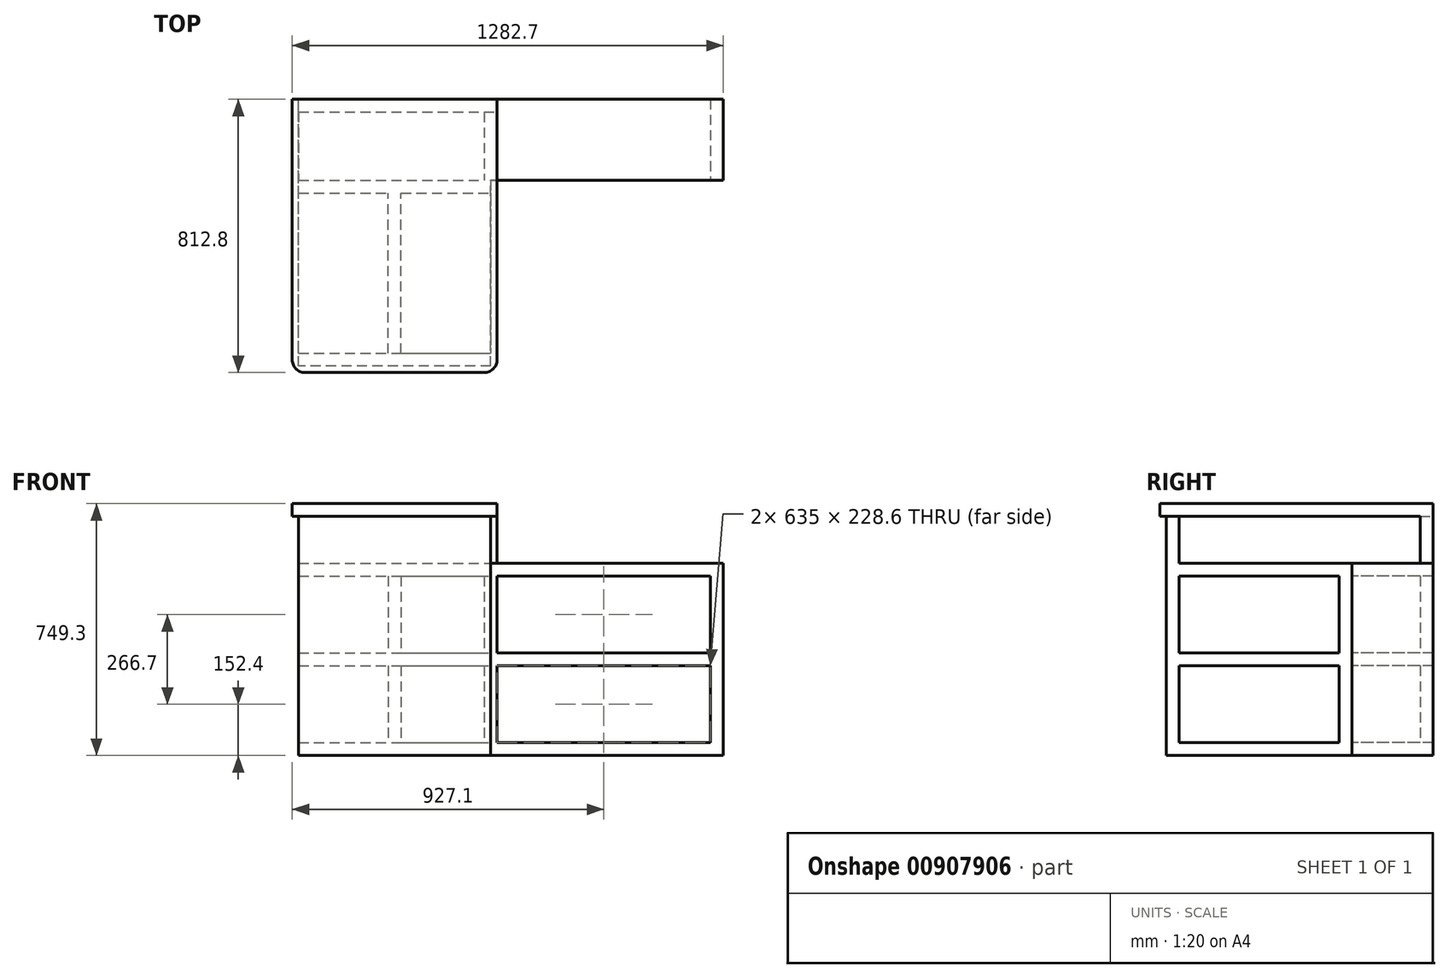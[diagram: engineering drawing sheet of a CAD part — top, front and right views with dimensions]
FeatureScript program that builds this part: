
annotation { "Feature Type Name" : "Feature", "Feature Type Description" : "" }
export const myFeature = defineFeature(function(context is Context, id is Id, definition is map)
    precondition{}
    {
        {
            var Q0;
            Q0=qCreatedBy(makeId("Top.planeOp"),FACE);
            var sketch = newSketch(context, id + "F0", { "sketchPlane" : qUnion([Q0])});
            skLineSegment(sketch, "E0.bottom", {"start": v(266.7, -406.4) * mm, "end": v(-266.7, -406.4) * mm});
            skLineSegment(sketch, "E0.top", {"start": v(304.8, 406.4) * mm, "end": v(-304.8, 406.4) * mm});
            skLineSegment(sketch, "E0.left", {"start": v(304.8, -368.3) * mm, "end": v(304.8, 165.1) * mm});
            skLineSegment(sketch, "E0.right", {"start": v(-304.8, -368.3) * mm, "end": v(-304.8, 406.4) * mm});
            skPoint(sketch, "E0.middle", {"position": v(0, 0) * mm});
            skLineSegment(sketch, "E1.bottom", {"start": v(304.8, 406.4) * mm, "end": v(977.9, 406.4) * mm});
            skLineSegment(sketch, "E1.top", {"start": v(304.8, 165.1) * mm, "end": v(977.9, 165.1) * mm});
            skLineSegment(sketch, "E1.right", {"start": v(977.9, 406.4) * mm, "end": v(977.9, 165.1) * mm});
            skLineSegment(sketch, "E2.0", {"start": v(958.85, 406.4) * mm, "end": v(958.85, 184.15) * mm});
            skLineSegment(sketch, "E2.1", {"start": v(-285.75, -387.35) * mm, "end": v(-285.75, 406.4) * mm});
            skLineSegment(sketch, "E2.2", {"start": v(285.75, -387.35) * mm, "end": v(-285.75, -387.35) * mm});
            skLineSegment(sketch, "E2.3", {"start": v(285.75, -387.35) * mm, "end": v(285.75, 184.15) * mm});
            skLineSegment(sketch, "E2.4", {"start": v(285.75, 184.15) * mm, "end": v(958.85, 184.15) * mm});
            skLineSegment(sketch, "E3.0", {"start": v(-330.2, -431.8) * mm, "end": v(-330.2, 406.4) * mm});
            skLineSegment(sketch, "E3.1", {"start": v(330.2, -431.8) * mm, "end": v(-330.2, -431.8) * mm});
            skLineSegment(sketch, "E3.2", {"start": v(330.2, -431.8) * mm, "end": v(330.2, 139.7) * mm});
            skLineSegment(sketch, "E3.3", {"start": v(330.2, 139.7) * mm, "end": v(977.9, 139.7) * mm});
            skLineSegment(sketch, "E4", {"start": v(977.9, 165.1) * mm, "end": v(977.9, 139.7) * mm});
            skLineSegment(sketch, "E5", {"start": v(304.8, 406.4) * mm, "end": v(304.8, 165.1) * mm});
            skLineSegment(sketch, "E6", {"start": v(-330.2, 406.4) * mm, "end": v(-304.8, 406.4) * mm});
            skPoint(sketch, "E7.visualSharp", {"position": v(-304.8, -406.4) * mm});
            skArc(sketch, "E7.filletArc", {"start": v(-304.8, -368.3) * mm, "mid": v(-293.64, -395.24) * mm, "end": v(-266.7, -406.4) * mm});
            skPoint(sketch, "E8.visualSharp", {"position": v(304.8, -406.4) * mm});
            skArc(sketch, "E8.filletArc", {"start": v(266.7, -406.4) * mm, "mid": v(293.64, -395.24) * mm, "end": v(304.8, -368.3) * mm});
            skLineSegment(sketch, "E9", {"start": v(305.02, 165.1) * mm, "end": v(285.75, 165.1) * mm});
            skSolve(sketch);
        }
        {
            var Q0;
            {var subQ4=sQuery(id+"F0.wireOp",EDGE,"E2.1");Q0=makeQuery(id+"F0.imprint","IMPRINT",FACE,{"disambiguationData":[TD([[makeQuery(id+"F0.imprint","IMPRINT",EDGE,{"derivedFrom":subQ4}),-1.0]])]});}
            var Q1;
            Q1=makeQuery(id+"F0.imprint","IMPRINT",FACE,{"disambiguationData":[TD([[makeQuery(id+"F0.imprint","IMPRINT",EDGE,{"derivedFrom":sQuery(id+"F0.wireOp",EDGE,"E0.bottom")}),-1.0]])]});
            extrude(context, id + "F1", {"entities" : qUnion([Q0, Q1]), "depth" : 38.1 * mm, "offsetDistance" : 25.4 * mm});
        }
        {
            var Q0;
            {var subQ4=sQuery(id+"F0.wireOp",EDGE,"E2.1");Q0=makeQuery(id+"F0.imprint","IMPRINT",FACE,{"disambiguationData":[TD([[makeQuery(id+"F0.imprint","IMPRINT",EDGE,{"derivedFrom":subQ4}),-1.0]])]});}
            extrude(context, id + "F2", {"entities" : qUnion([Q0]), "oppositeDirection" : true, "depth" : 711.2 * mm, "offsetDistance" : 25.4 * mm});
        }
        {
            var Q0;
            {var subQ3=sQuery(id+"F0.wireOp",EDGE,"E2.0");Q0=makeQuery(id+"F0.imprint","IMPRINT",FACE,{"disambiguationData":[TD([[makeQuery(id+"F0.imprint","IMPRINT",EDGE,{"derivedFrom":subQ3}),-1.0]])]});}
            var Q1;
            {var subQ2=sQuery(id+"F0.wireOp",EDGE,"E1.top");Q1=makeQuery(id+"F0.imprint","IMPRINT",FACE,{"disambiguationData":[TD([[makeQuery(id+"F0.imprint","IMPRINT",EDGE,{"derivedFrom":subQ2}),1.0]])]});}
            extrude(context, id + "F3", {"entities" : qUnion([Q0, Q1]), "oppositeDirection" : true, "depth" : 711.2 * mm, "offsetDistance" : 25.4 * mm});
        }
        {
            var Q0;
            Q0=qCreatedBy(makeId("Front.planeOp"),FACE);
            var sketch = newSketch(context, id + "F4", { "sketchPlane" : qUnion([Q0])});
            skLineSegment(sketch, "E10.bottom", {"start": v(977.9, 0) * mm, "end": v(304.8, 0) * mm});
            skLineSegment(sketch, "E10.top", {"start": v(977.9, -139.7) * mm, "end": v(304.8, -139.7) * mm});
            skLineSegment(sketch, "E10.left", {"start": v(977.9, 0) * mm, "end": v(977.9, -139.7) * mm});
            skLineSegment(sketch, "E10.right", {"start": v(304.8, 0) * mm, "end": v(304.8, -139.7) * mm});
            skLineSegment(sketch, "E11.bottom", {"start": v(304.8, -177.8) * mm, "end": v(939.8, -177.8) * mm});
            skLineSegment(sketch, "E11.top", {"start": v(304.8, -406.4) * mm, "end": v(939.8, -406.4) * mm});
            skLineSegment(sketch, "E11.left", {"start": v(304.8, -177.8) * mm, "end": v(304.8, -406.4) * mm});
            skLineSegment(sketch, "E11.right", {"start": v(939.8, -177.8) * mm, "end": v(939.8, -406.4) * mm});
            skLineSegment(sketch, "E12.bottom", {"start": v(304.8, -444.5) * mm, "end": v(939.8, -444.5) * mm});
            skLineSegment(sketch, "E12.top", {"start": v(304.8, -673.1) * mm, "end": v(939.8, -673.1) * mm});
            skLineSegment(sketch, "E12.left", {"start": v(304.8, -444.5) * mm, "end": v(304.8, -673.1) * mm});
            skLineSegment(sketch, "E12.right", {"start": v(939.8, -444.5) * mm, "end": v(939.8, -673.1) * mm});
            skSolve(sketch);
        }
        {
            var Q0;
            Q0=makeQuery(id+"F4.imprint","IMPRINT",FACE,{"disambiguationData":[TD([[makeQuery(id+"F4.imprint","IMPRINT",EDGE,{"derivedFrom":sQuery(id+"F4.wireOp",EDGE,"E10.bottom")}),1.0]])]});
            var Q1;
            Q1=makeQuery(id+"F4.imprint","IMPRINT",FACE,{"disambiguationData":[TD([[makeQuery(id+"F4.imprint","IMPRINT",EDGE,{"derivedFrom":sQuery(id+"F4.wireOp",EDGE,"E11.bottom")}),-1.0]])]});
            var Q2;
            Q2=makeQuery(id+"F4.imprint","IMPRINT",FACE,{"disambiguationData":[TD([[makeQuery(id+"F4.imprint","IMPRINT",EDGE,{"derivedFrom":sQuery(id+"F4.wireOp",EDGE,"E12.bottom")}),-1.0]])]});
            extrude(context, id + "F5", {"entities" : qUnion([Q0, Q1, Q2]), "operationType" : NewBodyOperationType.REMOVE, "endBound" : BoundingType.THROUGH_ALL, "oppositeDirection" : true, "depth" : 609.6 * mm, "offsetDistance" : 25.4 * mm});
        }
        {
            var Q0;
            {var subQ0=sQuery(id+"F0.wireOp",EDGE,"E2.4");var subQ1=sQuery(id+"F0.wireOp",EDGE,"E2.3");var subQ2=makeQuery(id+"F0.imprint","INTERSECT",VERTEX,{"derivedFrom":[subQ1,subQ0]});Q0=makeQuery(id+"F0.imprint","IMPRINT",FACE,{"disambiguationData":[TD([[makeQuery(id+"F0.imprint","IMPRINT",EDGE,{"disambiguationData":[TD([[subQ2,1.0]])],"derivedFrom":subQ1}),-1.0]])]});}
            extrude(context, id + "F6", {"entities" : qUnion([Q0]), "operationType" : NewBodyOperationType.ADD, "depth" : 38.1 * mm, "offsetDistance" : 25.4 * mm});
        }
        {
            var Q0;
            {var subQ0=sQuery(id+"F0.wireOp",EDGE,"E2.4");var subQ1=sQuery(id+"F0.wireOp",EDGE,"E2.3");var subQ2=makeQuery(id+"F0.imprint","INTERSECT",VERTEX,{"derivedFrom":[subQ1,subQ0]});Q0=makeQuery(id+"F0.imprint","IMPRINT",FACE,{"disambiguationData":[TD([[makeQuery(id+"F0.imprint","IMPRINT",EDGE,{"disambiguationData":[TD([[subQ2,1.0]])],"derivedFrom":subQ1}),-1.0]])]});}
            extrude(context, id + "F7", {"entities" : qUnion([Q0]), "operationType" : NewBodyOperationType.ADD, "oppositeDirection" : true, "depth" : 711.2 * mm, "offsetDistance" : 25.4 * mm});
        }
        {
            var Q0;
            Q0=qCreatedBy(makeId("Right.planeOp"),FACE);
            var sketch = newSketch(context, id + "F8", { "sketchPlane" : qUnion([Q0])});
            skLineSegment(sketch, "E13.bottom", {"start": v(-349.25, 0) * mm, "end": v(127, 0) * mm});
            skLineSegment(sketch, "E13.top", {"start": v(-349.25, -139.7) * mm, "end": v(127, -139.7) * mm});
            skLineSegment(sketch, "E13.left", {"start": v(-349.25, 0) * mm, "end": v(-349.25, -139.7) * mm});
            skLineSegment(sketch, "E13.right", {"start": v(127, 0) * mm, "end": v(127, -139.7) * mm});
            skLineSegment(sketch, "E14.bottom", {"start": v(-349.25, -177.8) * mm, "end": v(127, -177.8) * mm});
            skLineSegment(sketch, "E14.top", {"start": v(-349.25, -406.4) * mm, "end": v(127, -406.4) * mm});
            skLineSegment(sketch, "E14.left", {"start": v(-349.25, -177.8) * mm, "end": v(-349.25, -406.4) * mm});
            skLineSegment(sketch, "E14.right", {"start": v(127, -177.8) * mm, "end": v(127, -406.4) * mm});
            skLineSegment(sketch, "E15.bottom", {"start": v(-349.25, -444.5) * mm, "end": v(127, -444.5) * mm});
            skLineSegment(sketch, "E15.top", {"start": v(-349.25, -673.1) * mm, "end": v(127, -673.1) * mm});
            skLineSegment(sketch, "E15.left", {"start": v(-349.25, -444.5) * mm, "end": v(-349.25, -673.1) * mm});
            skLineSegment(sketch, "E15.right", {"start": v(127, -444.5) * mm, "end": v(127, -673.1) * mm});
            skLineSegment(sketch, "E16.bottom", {"start": v(127, -139.7) * mm, "end": v(368.3, -139.7) * mm});
            skLineSegment(sketch, "E16.top", {"start": v(127, 0) * mm, "end": v(368.3, 0) * mm});
            skLineSegment(sketch, "E16.left", {"start": v(127, -139.7) * mm, "end": v(127, 0) * mm});
            skLineSegment(sketch, "E16.right", {"start": v(368.3, -139.7) * mm, "end": v(368.3, 0) * mm});
            skSolve(sketch);
        }
        {
            var Q0;
            Q0 = qSketchRegion(id + "F8", true);
            extrude(context, id + "F9", {"entities" : qUnion([Q0]), "operationType" : NewBodyOperationType.REMOVE, "endBound" : BoundingType.SYMMETRIC, "oppositeDirection" : true, "depth" : 812.8 * mm, "offsetDistance" : 25.4 * mm});
        }
        {
            var Q0;
            Q0=qCreatedBy(makeId("Right.planeOp"),FACE);
            var sketch = newSketch(context, id + "F10", { "sketchPlane" : qUnion([Q0])});
            skLineSegment(sketch, "E17.bottom", {"start": v(368.3, -177.8) * mm, "end": v(165.1, -177.8) * mm});
            skLineSegment(sketch, "E17.top", {"start": v(368.3, -406.4) * mm, "end": v(165.1, -406.4) * mm});
            skLineSegment(sketch, "E17.left", {"start": v(368.3, -177.8) * mm, "end": v(368.3, -406.4) * mm});
            skLineSegment(sketch, "E17.right", {"start": v(165.1, -177.8) * mm, "end": v(165.1, -406.4) * mm});
            skLineSegment(sketch, "E18.bottom", {"start": v(368.3, -444.5) * mm, "end": v(165.1, -444.5) * mm});
            skLineSegment(sketch, "E18.top", {"start": v(368.3, -673.1) * mm, "end": v(165.1, -673.1) * mm});
            skLineSegment(sketch, "E18.left", {"start": v(368.3, -444.5) * mm, "end": v(368.3, -673.1) * mm});
            skLineSegment(sketch, "E18.right", {"start": v(165.1, -444.5) * mm, "end": v(165.1, -673.1) * mm});
            skSolve(sketch);
        }
        {
            var Q0;
            Q0 = qSketchRegion(id + "F10", true);
            extrude(context, id + "F11", {"entities" : qUnion([Q0]), "operationType" : NewBodyOperationType.REMOVE, "oppositeDirection" : true, "depth" : 609.6 * mm, "offsetDistance" : 25.4 * mm, "hasSecondDirection" : true, "secondDirectionBound" : SecondDirectionBoundingType.UP_TO_NEXT, "secondDirectionOppositeDirection" : false, "secondDirectionDepth" : 152.4 * mm, "hasSecondDirectionOffset" : true, "secondDirectionOffsetDistance" : 38.1 * mm});
        }
        {
            var Q0;
            Q0=qCreatedBy(makeId("Top.planeOp"),FACE);
            var sketch = newSketch(context, id + "F12", { "sketchPlane" : qUnion([Q0])});
            skLineSegment(sketch, "E19.bottom", {"start": v(19.05, 165.1) * mm, "end": v(-19.05, 165.1) * mm});
            skLineSegment(sketch, "E19.top", {"start": v(19.05, -387.35) * mm, "end": v(-19.05, -387.35) * mm});
            skLineSegment(sketch, "E19.left", {"start": v(19.05, 165.1) * mm, "end": v(19.05, -387.35) * mm});
            skLineSegment(sketch, "E19.right", {"start": v(-19.05, 165.1) * mm, "end": v(-19.05, -387.35) * mm});
            skSolve(sketch);
        }
        {
            var Q0;
            Q0 = qSketchRegion(id + "F12", true);
            extrude(context, id + "F13", {"entities" : qUnion([Q0]), "operationType" : NewBodyOperationType.ADD, "oppositeDirection" : true, "depth" : 711.2 * mm, "offsetDistance" : 25.4 * mm, "hasSecondDirection" : true, "secondDirectionOppositeDirection" : true, "secondDirectionDepth" : 152.4 * mm});
        }
    });
